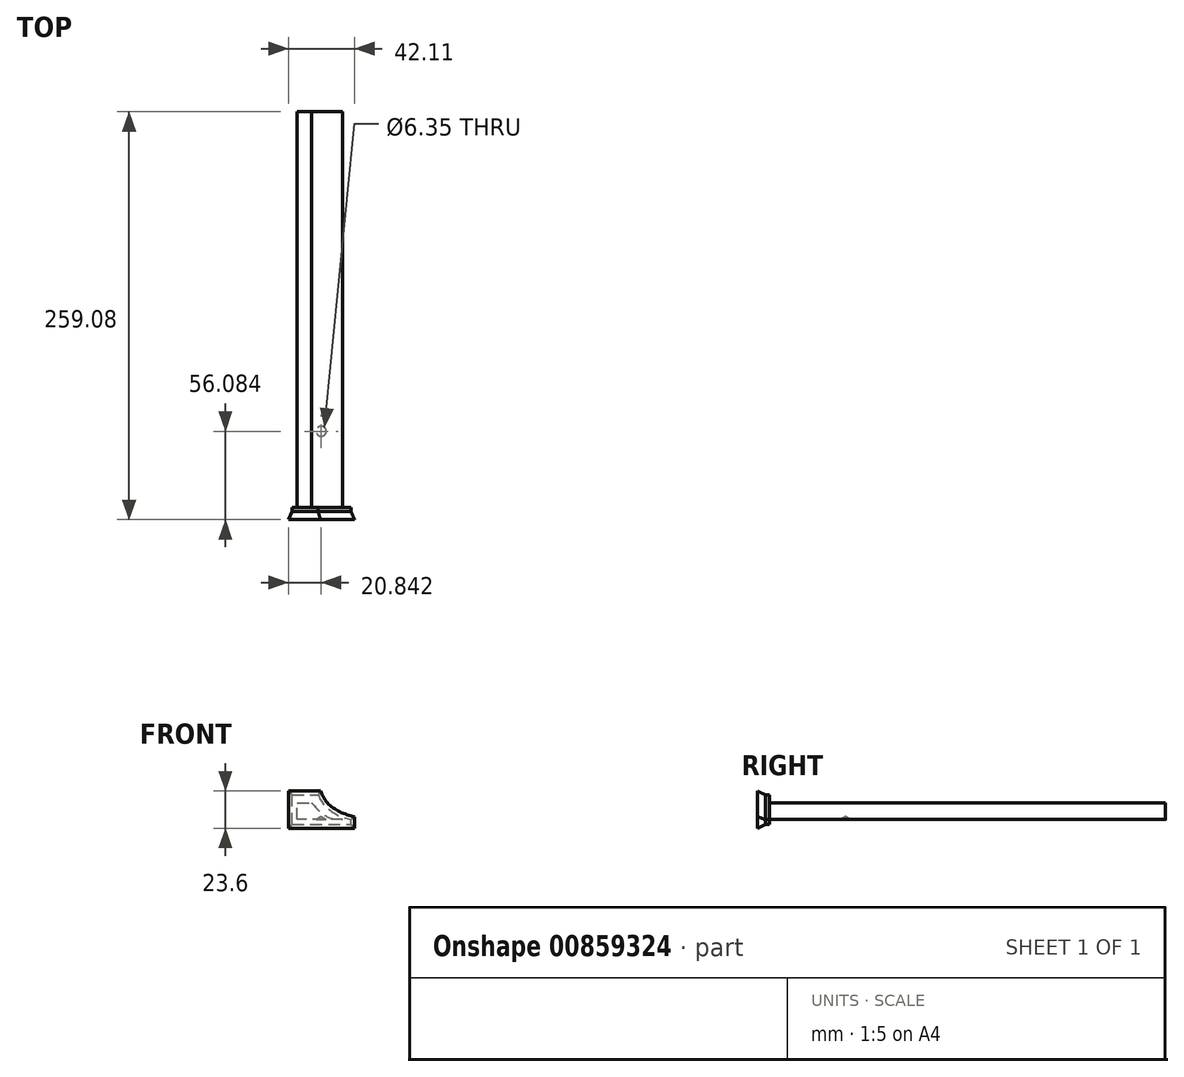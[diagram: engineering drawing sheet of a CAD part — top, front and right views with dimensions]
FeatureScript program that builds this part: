
annotation { "Feature Type Name" : "Feature", "Feature Type Description" : "" }
export const myFeature = defineFeature(function(context is Context, id is Id, definition is map)
    precondition{}
    {
        {
            var Q0;
            Q0=qCreatedBy(makeId("Front.planeOp"),FACE);
            var sketch = newSketch(context, id + "F0", { "sketchPlane" : qUnion([Q0])});
            skLineSegment(sketch, "E0", {"start": v(0, 0) * mm, "end": v(-28.95, 0) * mm});
            skLineSegment(sketch, "E1", {"start": v(-28.95, 0) * mm, "end": v(-28.95, 10.73) * mm});
            skLineSegment(sketch, "E2", {"start": v(-28.95, 10.73) * mm, "end": v(-19.7, 10.73) * mm});
            skFitSpline(sketch, "E3", {"points": [v(-19.7, 10.73) * mm, v(0, 0) * mm], "startDerivative": vector(21.09, -26.64) * mm, "endDerivative": vector(24.7, 0) * mm});
            skSolve(sketch);
        }
        {
            var Q0;
            Q0 = qSketchRegion(id + "F0", true);
            extrude(context, id + "F1", {"entities" : qUnion([Q0]), "endBound" : BoundingType.SYMMETRIC, "depth" : 254 * mm, "offsetDistance" : 25.4 * mm});
        }
        {
            var Q0;
            Q0=makeQuery(id+"F1.opExtrude","CAP_FACE",FACE,{"disambiguationData":[OSD([sQuery(id+"F0.wireOp",EDGE,"E0"),sQuery(id+"F0.wireOp",EDGE,"E1"),sQuery(id+"F0.wireOp",EDGE,"E2"),sQuery(id+"F0.wireOp",EDGE,"E3")])],"isStart":false});
            var sketch = newSketch(context, id + "F2", { "sketchPlane" : qUnion([Q0])});
            skLineSegment(sketch, "E4", {"start": v(-32.1, -3.14) * mm, "end": v(-32.1, 15.72) * mm});
            skLineSegment(sketch, "E5", {"start": v(-32.1, 15.72) * mm, "end": v(-15.63, 15.72) * mm});
            skFitSpline(sketch, "E6", {"points": [v(-15.63, 15.72) * mm, v(5.27, 0) * mm], "startDerivative": vector(10.54, -25.53) * mm, "endDerivative": vector(28.3, -6.66) * mm});
            skLineSegment(sketch, "E7", {"start": v(-32.1, -3.14) * mm, "end": v(5.27, -3.14) * mm});
            skLineSegment(sketch, "E8", {"start": v(5.27, -3.14) * mm, "end": v(5.27, 0) * mm});
            skSolve(sketch);
        }
        {
            var Q0;
            Q0 = qSketchRegion(id + "F2", true);
            extrude(context, id + "F3", {"entities" : qUnion([Q0]), "operationType" : NewBodyOperationType.ADD, "depth" : 5.08 * mm, "offsetDistance" : 25.4 * mm, "hasDraft" : true, "draftAngle" : 25 * degree, "hasSecondDirection" : true, "secondDirectionOppositeDirection" : true, "secondDirectionDepth" : 2.54 * mm});
        }
        {
            var Q0;
            Q0=makeQuery(id+"F1.opExtrude","SWEPT_FACE",FACE,{"disambiguationData":[OSD([sQuery(id+"F0.wireOp",EDGE,"E0")])]});
            var sketch = newSketch(context, id + "F4", { "sketchPlane" : qUnion([Q0])});
            skCircle(sketch, "E9", {"center": v(-13.63, 76) * mm, "radius": 3.35 * mm});
            skSolve(sketch);
        }
        {
            var Q0;
            Q0=sQuery(id+"F4.wireOp",VERTEX,"E9.center");
            var Q1;
            Q1=makeQuery(id+"F1.opExtrude","SWEPT_BODY",BODY,{"disambiguationData":[OSD([sQuery(id+"F0.wireOp",EDGE,"E0"),sQuery(id+"F0.wireOp",EDGE,"E1"),sQuery(id+"F0.wireOp",EDGE,"E2"),sQuery(id+"F0.wireOp",EDGE,"E3")])]});
            hole(context, id + "F5", {"style" : HoleStyle.SIMPLE, "endStyle" : HoleEndStyle.BLIND, "holeDiameter" : 6.35 * mm, "majorDiameter" : 6.35 * mm, "holeDepth" : 0.03 * mm, "isTappedThrough" : true, "tappedDepth" : 12.7 * mm, "tapClearance" : 3, "locations" : qUnion([Q0]), "scope" : qUnion([Q1])});
        }
    });
